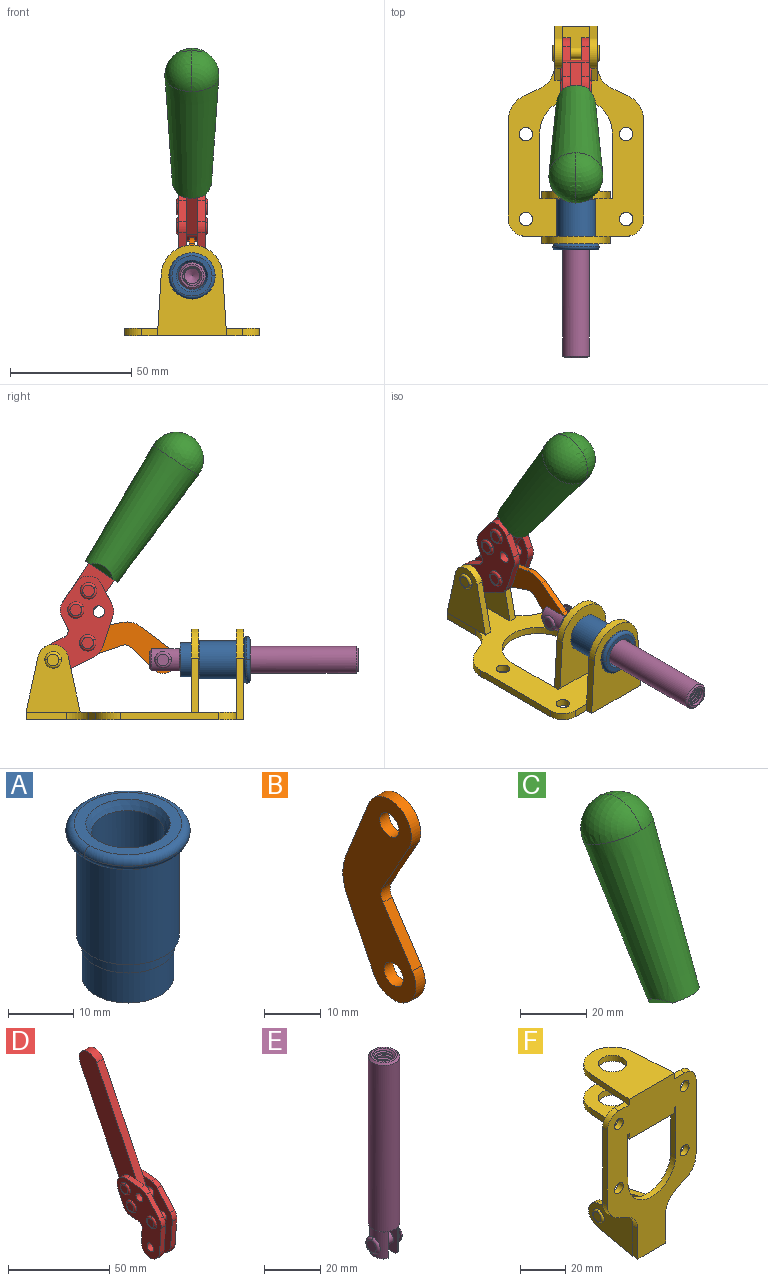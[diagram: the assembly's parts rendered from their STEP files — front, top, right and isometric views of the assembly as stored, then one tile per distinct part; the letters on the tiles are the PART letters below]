
ASSEMBLY  parts=6 mates=6
PART A: 15 faces, bbox 20.6x20.6x28.7 mm
  f0: torus R=8.26mm, axis (0,0,1), area 56.8mm2, adj f1,f10,f12
  f1: torus R=8.26mm, axis (0,0,1), area 56.8mm2, adj f0,f6,f13
  f2: cylinder r=5.59mm len=25.91mm, axis (0,0,1), area 909.6mm2, adj f3,f4
  f3: cone r=6.86mm half-angle=45deg, axis (0,0,-1), area 70.2mm2, adj f2,f14
  f4: cone r=6.47mm half-angle=30deg, axis (0,0,1), area 66.7mm2, adj f2,f13
  f5: cylinder r=7.04mm len=14.07mm, axis (0,0,1), area 252.6mm2, adj f11,f14
  f6: torus R=8.26mm, axis (0,0,1), area 56.8mm2, adj f1,f12,f13
  f7: cylinder r=7.16mm len=14.33mm, axis (0,0,1), area 91.5mm2, adj f9,f11
  f8: cylinder r=7.86mm len=18.42mm, axis (0,0,1), area 909.6mm2, adj f9,f10
  f9: plane 15.72x15.72mm, normal (0,0,-1), area 33mm2, adj f7,f8
  f10: plane 16.51x16.51mm, normal (0,0,-1), area 19.9mm2, adj f0,f8,f12
  f11: plane 14.33x14.33mm, normal (0,0,-1), area 5.7mm2, adj f5,f7
  f12: torus R=8.26mm, axis (0,0,1), area 56.8mm2, adj f0,f6,f10
  f13: plane 16.51x16.51mm, normal (0,0,1), area 82.7mm2, adj f1,f4,f6
  f14: plane 14.07x14.07mm, normal (0,0,-1), area 7.8mm2, adj f3,f5
PART B: 12 faces, bbox 2.3x18.2x42.8 mm
  f0: cylinder r=2.4mm len=4.8mm, axis (1,0,0), area 34.9mm2, adj f4,f11
  f1: cylinder r=10.41mm len=8.47mm, axis (1,0,0), area 20.2mm2, adj f4,f9,f10,f11
  f2: cylinder r=3.05mm len=3.16mm, axis (1,0,0), area 7.7mm2, adj f4,f6,f7,f11
  f3: cylinder r=2.4mm len=4.8mm, axis (1,0,0), area 34.9mm2, adj f4,f11
  f4: plane 42.81x18.23mm, normal (-1,0,0), area 414.1mm2, adj f0,f1,f2,f3,f5,f6,f7,f8
  f5: cylinder r=5.54mm len=10.67mm, axis (1,0,0), area 41.8mm2, adj f4,f6,f10,f11
  f6: plane 11.66x6.53mm, normal (0,-0.87,-0.49), area 30.9mm2, adj f2,f4,f5,f11
  f7: plane 11.17x7.33mm, normal (0,-0.84,0.55), area 30.9mm2, adj f2,f4,f8,f11
  f8: cylinder r=5.54mm len=10.51mm, axis (1,0,0), area 41.8mm2, adj f4,f7,f9,f11
  f9: plane 13.67x6.67mm, normal (0,0.9,-0.44), area 35.1mm2, adj f1,f4,f8,f11
  f10: plane 14.1x5.7mm, normal (0,0.93,0.37), area 35.1mm2, adj f1,f4,f5,f11
  f11: plane 42.81x18.23mm, normal (1,0,0), area 414.1mm2, adj f0,f1,f2,f3,f5,f6,f7,f8
PART C: 11 faces, bbox 22.3x42.6x64.5 mm
  f0: sphere r=11.13mm, area 411.4mm2, adj f1,f8
  f1: cone r=11.11mm half-angle=3.3deg, axis (0,0.44,0.9), area 3251.8mm2, adj f0,f7,f8,f9,f10
  f2: cylinder r=6.16mm len=11.7mm, axis (1,0,0), area 89.5mm2, adj f3,f4,f5,f6
  f3: plane 60.23x36.75mm, normal (-1,0,0), area 763.6mm2, adj f2,f4,f6,f10
  f4: plane 51.37x25.05mm, normal (0,0.9,-0.44), area 264.2mm2, adj f2,f3,f5,f10
  f5: plane 60.23x36.75mm, normal (1,0,0), area 763.6mm2, adj f2,f4,f6,f10
  f6: plane 51.37x25.05mm, normal (0,-0.9,0.44), area 264.2mm2, adj f2,f3,f5,f10
  f7: plane 9.95x5.95mm, normal (0.71,-0.31,-0.64), area 25.8mm2, adj f1,f10
  f8: sphere r=11.13mm, area 411.4mm2, adj f0,f1
  f9: plane 9.95x5.95mm, normal (-0.71,-0.31,-0.64), area 25.8mm2, adj f1,f10
  f10: plane 14.27x11.38mm, normal (0,-0.44,-0.9), area 106.7mm2, adj f1,f3,f4,f5,f6,f7,f9
PART D: 59 faces, bbox 12.9x60.2x99.6 mm
  f0: torus R=2.39mm, axis (-1,0,0), area 14.9mm2, adj f20,f43,f51
  f1: torus R=2.39mm, axis (-1,0,0), area 14.9mm2, adj f19,f42,f51
  f2: torus R=2.39mm, axis (-1,0,0), area 14.9mm2, adj f18,f35,f51
  f3: torus R=2.39mm, axis (-1,0,0), area 14.9mm2, adj f14,f17,f23
  f4: torus R=2.39mm, axis (-1,0,0), area 14.9mm2, adj f13,f16,f23
  f5: torus R=2.39mm, axis (-1,0,0), area 14.9mm2, adj f12,f15,f23
  f6: cylinder r=2.39mm len=4.78mm, axis (1,0,0), area 46.5mm2, adj f48,f50,f51
  f7: cylinder r=2.39mm len=4.78mm, axis (1,0,0), area 46.5mm2, adj f50,f51
  f8: cylinder r=6.35mm len=12.68mm, axis (1,0,0), area 61.8mm2, adj f38,f39,f50,f51
  f9: cylinder r=2.39mm len=4.78mm, axis (-1,0,0), area 70.5mm2, adj f46,f50
  f10: cylinder r=2.39mm len=4.78mm, axis (-1,0,0), area 46.5mm2, adj f23,f45,f46
  f11: cylinder r=2.39mm len=4.78mm, axis (-1,0,0), area 46.5mm2, adj f23,f46
  f12: plane 4.78x4.78mm, normal (1,0,0), area 17.9mm2, adj f5,f15
  f13: plane 4.78x4.78mm, normal (1,0,0), area 17.9mm2, adj f4,f16
  f14: plane 4.78x4.78mm, normal (1,0,0), area 17.9mm2, adj f3,f17
  f15: torus R=2.39mm, axis (-1,0,0), area 14.9mm2, adj f5,f12,f23
  f16: torus R=2.39mm, axis (-1,0,0), area 14.9mm2, adj f4,f13,f23
  f17: torus R=2.39mm, axis (-1,0,0), area 14.9mm2, adj f3,f14,f23
  f18: plane 4.78x4.78mm, normal (-1,0,0), area 17.9mm2, adj f2,f35
  f19: plane 4.78x4.78mm, normal (-1,0,0), area 17.9mm2, adj f1,f42
  f20: plane 4.78x4.78mm, normal (-1,0,0), area 17.9mm2, adj f0,f43
  f21: plane 2.26x0.2mm, normal (1,0,0), area 0.2mm2, adj f31,f44
  f22: plane 2.26x0.2mm, normal (-1,0,0), area 0.2mm2, adj f41,f44
  f23: plane 39.37x30.77mm, normal (1,0,0), area 565.5mm2, adj f3,f4,f5,f10,f11,f15,f16,f17
  f24: cylinder r=6.1mm len=4.15mm, axis (-1,0,0), area 14.7mm2, adj f23,f25,f32,f46
  f25: plane 10.25x9.01mm, normal (0,-0.75,0.66), area 42.3mm2, adj f23,f24,f26,f46
  f26: cylinder r=6.35mm len=4.64mm, axis (-1,0,0), area 15.6mm2, adj f23,f25,f27,f46
  f27: plane 15.84x3.1mm, normal (0,-1,-0.07), area 49.2mm2, adj f23,f26,f28,f46
  f28: cylinder r=6.35mm len=12.68mm, axis (-1,0,0), area 61.8mm2, adj f23,f27,f29,f46
  f29: plane 8.11x3.1mm, normal (0,1,0.07), area 25.2mm2, adj f23,f28,f30,f46
  f30: cylinder r=3.05mm len=3.25mm, axis (-1,0,0), area 14.8mm2, adj f23,f29,f31,f46
  f31: plane 5.99x3.1mm, normal (0,0.07,-1), area 18.6mm2, adj f21,f23,f30,f44,f46
  f32: plane 9.5x3.1mm, normal (0,-0.07,1), area 29.5mm2, adj f23,f24,f33,f46,f47
  f33: cylinder r=6.1mm len=8.63mm, axis (-1,0,0), area 39.1mm2, adj f23,f32,f34,f47
  f34: plane 8.65x3.96mm, normal (0,0.91,-0.42), area 29.5mm2, adj f23,f33,f44,f47
  f35: torus R=2.39mm, axis (-1,0,0), area 14.9mm2, adj f2,f18,f51
  f36: plane 10.25x9.01mm, normal (0,-0.75,0.66), area 42.3mm2, adj f37,f49,f50,f51
  f37: cylinder r=6.35mm len=4.64mm, axis (1,0,0), area 15.6mm2, adj f36,f38,f50,f51
  f38: plane 15.84x3.1mm, normal (0,-1,-0.07), area 49.2mm2, adj f8,f37,f50,f51
  f39: plane 8.11x3.1mm, normal (0,1,0.07), area 25.2mm2, adj f8,f40,f50,f51
  f40: cylinder r=3.05mm len=3.25mm, axis (1,0,0), area 14.8mm2, adj f39,f41,f50,f51
  f41: plane 5.99x3.1mm, normal (0,0.07,-1), area 18.6mm2, adj f22,f40,f44,f50,f51
  f42: torus R=2.39mm, axis (-1,0,0), area 14.9mm2, adj f1,f19,f51
  f43: torus R=2.39mm, axis (-1,0,0), area 14.9mm2, adj f0,f20,f51
  f44: cylinder r=6.35mm len=12.12mm, axis (-1,0,0), area 128.9mm2, adj f21,f22,f23,f31,f34,f41,f46,f47
  f45: plane 2.65x1.35mm, normal (1,0,0), area 1mm2, adj f10,f55
  f46: plane 39.08x20.42mm, normal (-1,0,0), area 412.5mm2, adj f9,f10,f11,f24,f25,f26,f27,f28
  f47: plane 77.62x39.82mm, normal (1,0,0), area 850mm2, adj f32,f33,f34,f44,f53,f54,f55
  f48: plane 2.65x1.35mm, normal (-1,0,0), area 1mm2, adj f6,f55
  f49: cylinder r=6.1mm len=4.15mm, axis (1,0,0), area 14.7mm2, adj f36,f50,f51,f56
  f50: plane 39.08x20.42mm, normal (1,0,0), area 412.5mm2, adj f6,f7,f8,f9,f36,f37,f38,f39
  f51: plane 39.37x30.77mm, normal (-1,0,0), area 565.5mm2, adj f0,f1,f2,f6,f7,f8,f35,f36
  f52: plane 8.65x3.96mm, normal (0,0.91,-0.42), area 29.5mm2, adj f44,f51,f57,f58
  f53: plane 68.49x33.4mm, normal (0,0.9,-0.44), area 358.1mm2, adj f44,f47,f54,f58
  f54: cylinder r=6.35mm len=12.06mm, axis (1,0,0), area 93.7mm2, adj f47,f53,f55,f58
  f55: plane 68.49x33.4mm, normal (0,-0.9,0.44), area 358.1mm2, adj f44,f45,f46,f47,f48,f50,f54,f58
  f56: plane 9.5x3.1mm, normal (0,-0.07,1), area 29.5mm2, adj f49,f50,f51,f57,f58
  f57: cylinder r=6.1mm len=8.63mm, axis (1,0,0), area 39.1mm2, adj f51,f52,f56,f58
  f58: plane 77.62x39.82mm, normal (-1,0,0), area 850mm2, adj f44,f52,f53,f54,f55,f56,f57
PART E: 48 faces, bbox 12.6x11.1x86.1 mm
  f0: torus R=2.41mm, axis (-1,0,0), area 15mm2, adj f30,f32,f34
  f1: torus R=2.41mm, axis (-1,0,0), area 15mm2, adj f29,f31,f33
  f2: cylinder r=5.54mm len=72.39mm, axis (0,0,1), area 2518.5mm2, adj f3,f4,f42,f43
  f3: cone r=5.54mm half-angle=45deg, axis (0,0,1), area 7.6mm2, adj f2,f5,f41
  f4: cone r=5.54mm half-angle=45deg, axis (0,0,-1), area 34.9mm2, adj f2,f39
  f5: cylinder r=5.08mm len=11.48mm, axis (0,0,1), area 108.3mm2, adj f3,f7,f8,f41
  f6: cylinder r=2.41mm len=4.83mm, axis (-1,0,0), area 71.2mm2, adj f40,f41
  f7: cylinder r=2.41mm len=4.83mm, axis (-1,0,0), area 7.6mm2, adj f5,f34
  f8: cone r=5.08mm half-angle=45deg, axis (0,0,1), area 10.6mm2, adj f5,f37,f41
  f9: cone r=3.98mm half-angle=45deg, axis (0,0,1), area 17.6mm2, adj f27,f39,f45,f46,f47
  f10: cylinder r=2.41mm len=4.83mm, axis (-1,0,0), area 7.6mm2, adj f33,f38
  f11: cylinder r=3.2mm len=6.4mm, axis (0,0,1), area 78.4mm2, adj f12,f28,f44,f45,f47
  f12: cylinder r=3.2mm len=6.4mm, axis (0,0,1), area 10.5mm2, adj f11,f13,f45,f47
  f13: cylinder r=3.2mm len=6.4mm, axis (0,0,1), area 10.5mm2, adj f12,f14,f45,f47
  f14: cylinder r=3.2mm len=6.4mm, axis (0,0,1), area 10.5mm2, adj f13,f15,f45,f47
  f15: cylinder r=3.2mm len=6.4mm, axis (0,0,1), area 10.5mm2, adj f14,f16,f45,f47
  f16: cylinder r=3.2mm len=6.4mm, axis (0,0,1), area 10.5mm2, adj f15,f17,f45,f47
  f17: cylinder r=3.2mm len=6.4mm, axis (0,0,1), area 10.5mm2, adj f16,f18,f45,f47
  f18: cylinder r=3.2mm len=6.4mm, axis (0,0,1), area 10.5mm2, adj f17,f19,f45,f47
  f19: cylinder r=3.2mm len=6.4mm, axis (0,0,1), area 10.5mm2, adj f18,f20,f45,f47
  f20: cylinder r=3.2mm len=6.4mm, axis (0,0,1), area 10.5mm2, adj f19,f21,f45,f47
  f21: cylinder r=3.2mm len=6.4mm, axis (0,0,1), area 10.5mm2, adj f20,f22,f45,f47
  f22: cylinder r=3.2mm len=6.4mm, axis (0,0,1), area 10.5mm2, adj f21,f23,f45,f47
  f23: cylinder r=3.2mm len=6.4mm, axis (0,0,1), area 10.5mm2, adj f22,f24,f45,f47
  f24: cylinder r=3.2mm len=6.4mm, axis (0,0,1), area 10.5mm2, adj f23,f25,f45,f47
  f25: cylinder r=3.2mm len=6.4mm, axis (0,0,1), area 10.5mm2, adj f24,f26,f45,f47
  f26: cylinder r=3.2mm len=6.4mm, axis (0,0,1), area 10.5mm2, adj f25,f27,f45,f47
  f27: cylinder r=3.2mm len=6.4mm, axis (0,0,1), area 7.4mm2, adj f9,f26,f45,f47
  f28: cone r=3.2mm half-angle=60deg, axis (0,0,1), area 37.2mm2, adj f11
  f29: plane 4.83x4.83mm, normal (-1,0,0), area 18.3mm2, adj f1,f31
  f30: plane 4.83x4.83mm, normal (1,0,0), area 18.3mm2, adj f0,f32
  f31: torus R=2.41mm, axis (-1,0,0), area 15mm2, adj f1,f29,f33
  f32: torus R=2.41mm, axis (-1,0,0), area 15mm2, adj f0,f30,f34
  f33: plane 6.83x6.83mm, normal (1,0,0), area 18.3mm2, adj f1,f10,f31
  f34: plane 6.83x6.83mm, normal (-1,0,0), area 18.3mm2, adj f0,f7,f32
  f35: cone r=5.08mm half-angle=45deg, axis (0,0,1), area 10.6mm2, adj f36,f38,f40
  f36: plane 7.25x1.97mm, normal (0,0,-1), area 10mm2, adj f35,f40
  f37: plane 7.25x1.97mm, normal (0,0,-1), area 10mm2, adj f8,f41
  f38: cylinder r=5.08mm len=11.48mm, axis (0,0,1), area 108.3mm2, adj f10,f35,f40,f42
  f39: plane 9.55x9.55mm, normal (0,0,1), area 22mm2, adj f4,f9
  f40: plane 12.76x10.09mm, normal (1,0,0), area 95.7mm2, adj f6,f35,f36,f38,f42,f43
  f41: plane 12.76x10.09mm, normal (-1,0,0), area 95.7mm2, adj f3,f5,f6,f8,f37,f43
  f42: cone r=5.54mm half-angle=45deg, axis (0,0,1), area 7.6mm2, adj f2,f38,f40
  f43: plane 11.07x4.7mm, normal (0,0,-1), area 50.4mm2, adj f2,f40,f41
  f44: plane 0.89x0.62mm, normal (-1,0,0), area 0.3mm2, adj f11,f45,f46,f47
  f45: bspline ~24.8x7.63mm, area 266.6mm2, adj f9,f11,f12,f13,f14,f15,f16,f17
  f46: bspline ~24.87x7.63mm, area 73.6mm2, adj f9,f44,f45,f47
  f47: bspline ~24.98x7.63mm, area 272.5mm2, adj f9,f11,f12,f13,f14,f15,f16,f17
PART F: 55 faces, bbox 55.7x37.4x89.8 mm
  f0: torus R=2.41mm, axis (-1,0,0), area 15mm2, adj f11,f15,f25
  f1: torus R=2.41mm, axis (-1,0,0), area 15mm2, adj f10,f12,f22
  f2: cylinder r=2.78mm len=5.56mm, axis (0,-1,0), area 54.2mm2, adj f30,f54
  f3: cylinder r=14.99mm len=29.97mm, axis (0,-1,0), area 145.9mm2, adj f30,f49,f53,f54
  f4: cylinder r=2.78mm len=5.56mm, axis (0,-1,0), area 54.2mm2, adj f30,f54
  f5: cylinder r=2.78mm len=5.56mm, axis (0,-1,0), area 54.2mm2, adj f30,f54
  f6: cylinder r=2.78mm len=5.56mm, axis (0,-1,0), area 54.2mm2, adj f30,f54
  f7: cylinder r=6.35mm len=12.7mm, axis (0,0,1), area 123.6mm2, adj f27,f51
  f8: cylinder r=6.35mm len=12.7mm, axis (0,0,-1), area 124.7mm2, adj f21,f35
  f9: cylinder r=2.41mm len=11.18mm, axis (-1,0,0), area 169.4mm2, adj f16,f19
  f10: plane 4.83x4.83mm, normal (1,0,0), area 18.3mm2, adj f1,f12
  f11: plane 4.83x4.83mm, normal (-1,0,0), area 18.3mm2, adj f0,f15
  f12: torus R=2.41mm, axis (-1,0,0), area 15mm2, adj f1,f10,f22
  f13: cylinder r=6.35mm len=12.41mm, axis (1,0,0), area 53.4mm2, adj f18,f19,f22,f23
  f14: cylinder r=6.35mm len=12.41mm, axis (-1,0,0), area 53.4mm2, adj f16,f17,f24,f25
  f15: torus R=2.41mm, axis (-1,0,0), area 15mm2, adj f0,f11,f25
  f16: plane 27.86x22.35mm, normal (1,0,0), area 425.4mm2, adj f9,f14,f17,f24,f30
  f17: plane 22.86x4.97mm, normal (0,0.21,0.98), area 72.5mm2, adj f14,f16,f25,f30
  f18: plane 22.86x4.97mm, normal (0,0.21,0.98), area 72.5mm2, adj f13,f19,f22,f30
  f19: plane 27.86x22.35mm, normal (-1,0,0), area 425.4mm2, adj f9,f13,f18,f23,f30
  f20: cylinder r=12.7mm len=25.35mm, axis (0,0,-1), area 119.8mm2, adj f21,f34,f35,f36
  f21: plane 34.21x28.07mm, normal (0,0,-1), area 702.4mm2, adj f8,f20,f30,f34,f36
  f22: plane 27.96x22.45mm, normal (1,0,0), area 407.2mm2, adj f1,f12,f13,f18,f23,f30,f42,f43
  f23: plane 22.86x4.97mm, normal (0,0.21,-0.98), area 72.5mm2, adj f13,f19,f22,f44
  f24: plane 22.86x4.97mm, normal (0,0.21,-0.98), area 72.5mm2, adj f14,f16,f25,f44
  f25: plane 27.86x22.35mm, normal (-1,0,0), area 407.1mm2, adj f0,f14,f15,f17,f24,f30,f45,f46
  f26: plane 3.1x0.95mm, normal (0,0,-1), area 2.7mm2, adj f30,f49,f50,f54
  f27: plane 34.21x28.07mm, normal (0,0,1), area 702.4mm2, adj f7,f28,f30,f50,f52
  f28: cylinder r=12.7mm len=25.35mm, axis (0,0,1), area 118.8mm2, adj f27,f50,f51,f52
  f29: plane 3.1x0.95mm, normal (0,0,-1), area 2.7mm2, adj f30,f52,f53,f54
  f30: plane 86.54x55.63mm, normal (0,1,0), area 2362.9mm2, adj f2,f3,f4,f5,f6,f16,f17,f18
  f31: plane 40.56x3.1mm, normal (-1,0,0), area 125.7mm2, adj f30,f32,f48,f54
  f32: cylinder r=7.11mm len=7.11mm, axis (0,-1,0), area 34.6mm2, adj f30,f31,f33,f54
  f33: plane 6.67x3.1mm, normal (0,0,1), area 20.4mm2, adj f30,f32,f34,f54
  f34: plane 25.39x3.13mm, normal (-1,0.06,0), area 79.5mm2, adj f20,f21,f33,f35,f54
  f35: plane 37.31x28.45mm, normal (0,0,1), area 789.9mm2, adj f8,f20,f34,f36,f54
  f36: plane 25.39x3.13mm, normal (1,0.06,0), area 79.5mm2, adj f20,f21,f35,f37,f54
  f37: plane 6.67x3.1mm, normal (0,0,1), area 20.4mm2, adj f30,f36,f38,f54
  f38: cylinder r=7.11mm len=7.11mm, axis (0,-1,0), area 34.6mm2, adj f30,f37,f39,f54
  f39: plane 40.56x3.1mm, normal (1,0,0), area 125.7mm2, adj f30,f38,f40,f54
  f40: cylinder r=11.18mm len=10.16mm, axis (0,-1,0), area 39.5mm2, adj f30,f39,f41,f54
  f41: plane 6.09x3.1mm, normal (0.42,0,-0.91), area 20.8mm2, adj f30,f40,f42,f54
  f42: cylinder r=11.18mm len=9.41mm, axis (0,-1,0), area 37.2mm2, adj f22,f30,f41,f43,f54
  f43: plane 16.5x3.1mm, normal (1,0,0), area 51.1mm2, adj f22,f42,f44,f54
  f44: plane 17.37x3.1mm, normal (0,0,-1), area 53.8mm2, adj f23,f24,f30,f43,f45,f54
  f45: plane 16.5x3.1mm, normal (-1,0,0), area 51.1mm2, adj f25,f44,f46,f54
  f46: cylinder r=11.18mm len=9.41mm, axis (0,-1,0), area 37.2mm2, adj f25,f30,f45,f47,f54
  f47: plane 6.09x3.1mm, normal (-0.42,0,-0.91), area 20.8mm2, adj f30,f46,f48,f54
  f48: cylinder r=11.18mm len=10.16mm, axis (0,-1,0), area 39.5mm2, adj f30,f31,f47,f54
  f49: plane 26.54x3.1mm, normal (-1,0,0), area 82.3mm2, adj f3,f26,f30,f54
  f50: plane 25.39x3.1mm, normal (1,0.06,0), area 78.8mm2, adj f26,f27,f28,f51,f54
  f51: plane 37.31x28.45mm, normal (0,0,-1), area 789.9mm2, adj f7,f28,f50,f52,f54
  f52: plane 25.39x3.1mm, normal (-1,0.06,0), area 78.8mm2, adj f27,f28,f29,f51,f54
  f53: plane 26.54x3.1mm, normal (1,0,0), area 82.3mm2, adj f3,f29,f30,f54
  f54: plane 89.66x55.63mm, normal (0,-1,0), area 2678.5mm2, adj f2,f3,f4,f5,f6,f26,f29,f31
PLACE A rot(axis=(1,0,0),90deg) t=(0,0,0)mm
PLACE B rot(axis=(1,0,0),104.8deg) t=(0,8.14,4.76)mm
PLACE C rot(axis=(1,0,0),59.7deg) t=(-0.04,-8.03,19.53)mm
PLACE D rot(axis=(1,0,0),59.7deg) t=(0,-8.03,19.53)mm
PLACE E rot(axis=(1,0,0),90deg) t=(0,2.37,0)mm
PLACE F rot(axis=(1,0,0),90deg) t=(0,0,0)mm fixed
MATE revolute B.f3 <-> D.f4  axis (1,0,0) through (0,17.86,31.64)mm
MATE slider E.f2 <-> A.f2  axis (0,-1,0) through (0,-56.41,24.61)mm
MATE fastened C.f2 <-> D.f54  axis (1,0,0) through (-2.35,-19.53,108.5)mm
MATE revolute D.f7 <-> F.f0  axis (1,0,0) through (0,32.09,24.61)mm
MATE fastened F.f7 <-> A.f2  axis (0,-1,0) through (0,-46.39,24.61)mm
MATE revolute B.f5 <-> E.f6  axis (1,0,0) through (0,-13.11,24.61)mm
